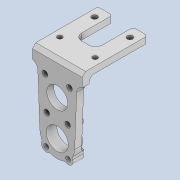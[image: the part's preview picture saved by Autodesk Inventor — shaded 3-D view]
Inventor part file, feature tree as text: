
AUTODESK INVENTOR PART (.ipt)
format: ipt  version: 2020 (Build 240168000, 168)  size: 437,248 bytes
history: native  units: mm
features: projected_geometry x14, sketch x11, extrude x10, reference x10, fillet x7, other x6, chamfer x2, hole x1, thicken_offset x1
ambient origin geometry x8: Origin, YZ Plane, XZ Plane, XY Plane, X Axis, Y Axis, Z Axis, Center Point
bodies: Solid1 (feature_tree)
feature tree (62):
  extrude  "Extrusion1"  Depth=6.0mm
  extrude  "Extrusion2"  Depth=10.0mm
  extrude  "Extrusion3"  Depth=1.5mm
  extrude  "Extrusion4"  Depth=4.15mm
  extrude  "Extrusion5"  Depth=4.15mm
  extrude  "Extrusion6"  Depth=6.0mm TaperAngle=0.0deg
  fillet  "Fillet1"  Radius=17.5mm
  fillet  "Fillet2"  Radius=6.0mm
  chamfer  "Chamfer1"  Distance=6.0mm
  fillet  "Fillet3"  Radius=8.5mm
  fillet  "Fillet4"  Radius=1.0mm
  fillet  "Fillet5"  Radius=1.0mm
  extrude  "Extrusion8"  Depth=3.0mm
  hole  "Hole1"  [1 undecoded]
  fillet  "Fillet6"  Radius=1.5mm
  extrude  "Extrusion9"  Depth=3.0mm
  thicken_offset  "Thicken1"
  chamfer  "Chamfer2"  Distance=2.0mm
  extrude  "Extrusion10"  Depth=6.0mm
  fillet  "Fillet7"  Radius=6.0mm
  extrude  "Extrusion11"  TaperAngle=30.0deg  [1 undecoded]
  sketch  "Sketch1"  dims[d0=6.0mm d1=6.0mm]
  reference  "Reference1"
  reference  "Reference2"
  reference  "Reference3"
  reference  "Reference4"
  reference  "Reference5"
  sketch  "Sketch2"  dims[d2=8.5mm d3=10.0mm]
  projected_geometry  "Projected Loop1"
  reference  "Reference6"
  sketch  "Sketch3"  dims[d4=1.5mm d5=1.5mm]
  reference  "Reference7"
  projected_geometry  "Projected Loop2"
  projected_geometry  "Projected Loop3"
  projected_geometry  "Projected Loop4"
  sketch  "Sketch4"  dims[d6=2.0mm d7=0.0mm d8=4.15mm]
  projected_geometry  "Projected Loop5"
  sketch  "Sketch5"  dims[d9=18.8mm d10=4.15mm]
  projected_geometry  "Projected Loop6"
  reference  "Reference8"
  reference  "Reference9"
  sketch  "Sketch6"  dims[d11=18.8mm d12=1.8mm d13=0.0mm d14=17.5mm d15=6.0mm d16=0.0mm]
  reference  "Reference10"
  sketch  "Sketch8"  dims[d17=3.0mm]
  projected_geometry  "Projected Loop7"
  sketch  "Sketch9"  dims[d18=1.6mm]
  projected_geometry  "Projected Loop8"
  projected_geometry  "Projected Loop9"
  projected_geometry  "Projected Loop10"
  sketch  "Sketch10"  dims[d19=3.0mm]
  projected_geometry  "Projected Loop11"
  projected_geometry  "Projected Loop12"
  sketch  "Sketch11"  dims[d20=1.6mm d21=6.0mm d22=0.0mm d23=8.5mm d24=1.0mm d25=0.0mm d26=1.0mm d27=0.0mm]
  projected_geometry  "Projected Loop13"
  sketch  "Sketch12"  dims[d30=1.0mm d31=1.5mm d32=1.0mm d33=2.0mm d34=45.0deg d35=1.5mm d36=2.0mm d37=2.0mm d38=6.0mm d39=6.0mm d40=30.0deg d41=30.0deg d42=5.5mm d43=5.5mm d44=6.981317mm d45=6.981317mm d46=3.0mm d47=3.0mm d48=3.0mm d49=3.0mm d50=3.0mm d51=3.0mm d52=1.0mm d53=0.0mm d54=1.6mm d55=6.0mm d56=4.0mm d57=2.0mm d58=90.0deg d59=5.0mm d60=0.0mm d61=1.0mm d62=10.15mm d63=10.0mm d64=1.4mm d65=1.4mm d66=3.0mm d67=0.0mm d68=0.15mm d69=0.15mm d70=0.5mm d71=2.0mm d72=45.0deg d73=7.330383mm d74=7.330383mm d75=0.3mm d76=2.8mm d77=0.3mm d78=2.8mm d79=3.0mm d80=0.0mm d81=1.0mm d82=1.4mm d83=1.4mm d84=3.0mm d85=0.0mm]
  projected_geometry  "Projected Loop14"
  parser-record x1  (decoder bookkeeping rows leaked as tree rows — omitted from the tree; the rows remain in map.json)
  other  "tip_ass_t1.iam"
  other  "motor_1608:1"
  other  "motor_1608_outer:1"
  other  "bearing_3_6_2:3"
  other  "pin_conn_1:1"
note: 2 required parameter values undecoded (feature->parameter linkage not recoverable at this tier; creation-order binding heuristic only, values carry confidence <= 0.55)
note: 1 file-system path scrubbed to <path> (originals preserved in map.json)
